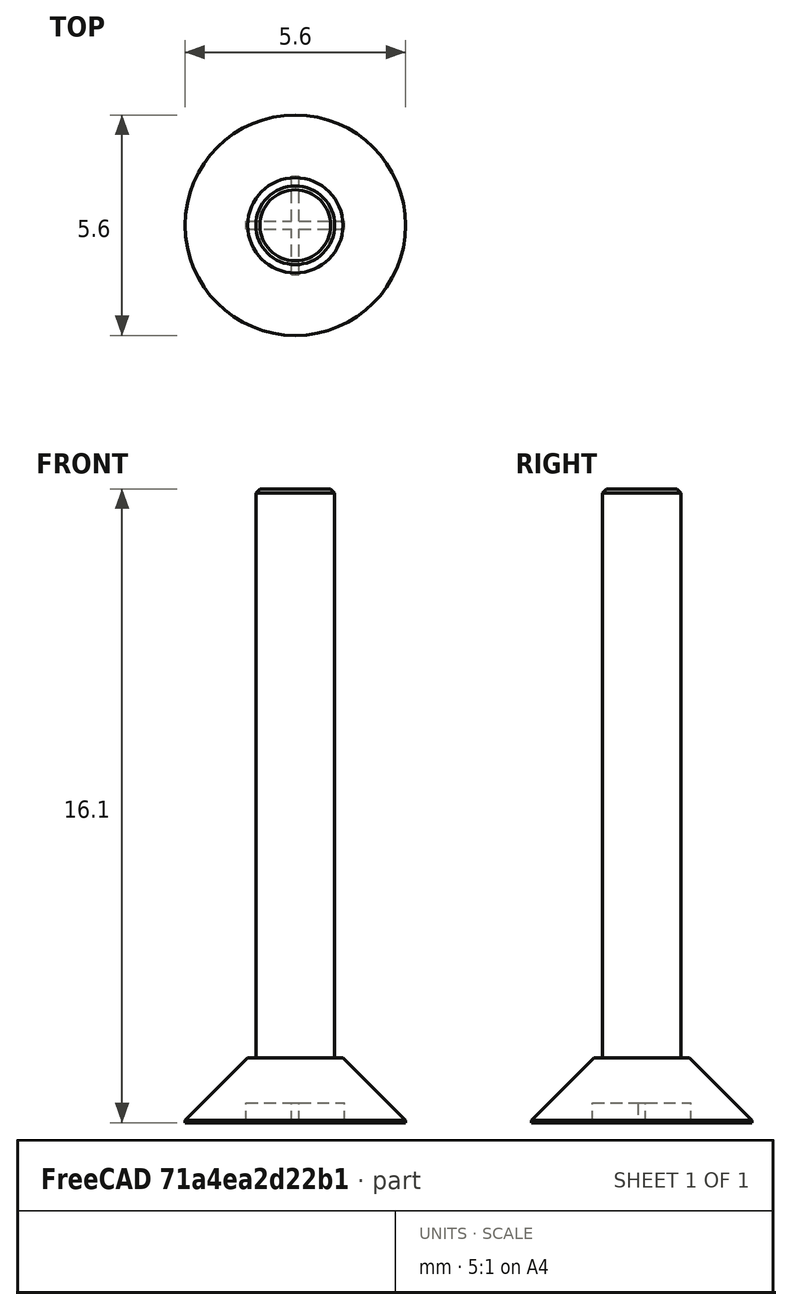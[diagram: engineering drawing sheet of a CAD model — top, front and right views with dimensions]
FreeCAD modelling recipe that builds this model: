
FCSTD DOCUMENT  (FreeCAD 0.16R6706 (Git))
Label: Screw_M3x16
License: All rights reserved
LicenseURL: http://en.wikipedia.org/wiki/All_rights_reserved
objects: Part::Cylinder×2, Part::Box×2, Part::MultiFuse×2, PartDesign::Chamfer×2, Part::Cut×1
note: 9 computed .brp shape members not serialized (recipe doc carries the construction recipe); baked Part::Feature solids carry a one-line shape summary decoded from their .brp

FEATURE [Part::Cylinder] Cylinder  label="Zylinder"
  Angle = 360
  Height = 1.65
  Radius = 2.8
FEATURE [Part::Cylinder] Cylinder001  label="Zylinder001"
  Angle = 360
  Height = 16
  Placement = pos=(0,0,0.1) rot=(0,0,1;0rad)
  Radius = 1
FEATURE [Part::Box] Box  label="Würfel"
  Height = 0.5
  Length = 0.2
  Placement = pos=(-0.1,-1.25,0) rot=(0,0,1;0rad)
  Width = 2.5
FEATURE [Part::Box] Box001  label="Würfel001"
  Height = 0.5
  Length = 2.5
  Placement = pos=(-1.25,-0.1,0) rot=(0,0,1;0rad)
  Width = 0.2
FEATURE [Part::MultiFuse] Fusion
  Shapes = -> [Box001,Box]
FEATURE [Part::MultiFuse] Fusion001
  Shapes = -> [Cylinder001,Cylinder]
FEATURE [Part::Cut] Cut
  Base = -> Fusion001
  Tool = -> Fusion
FEATURE [PartDesign::Chamfer] Chamfer
  Base = -> Cut [Edge4]
  Size = 1.59
FEATURE [PartDesign::Chamfer] Chamfer001  label="SCREW"
  Base = -> Chamfer [Edge6]
  Size = 0.1
